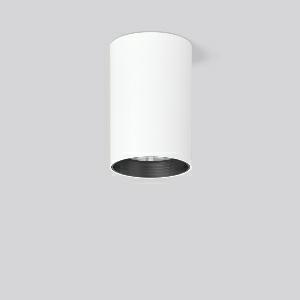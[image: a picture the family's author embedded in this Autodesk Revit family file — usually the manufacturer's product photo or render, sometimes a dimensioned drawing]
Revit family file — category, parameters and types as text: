
# Revit family: heledon_maxi_a_931229_002_3_b1d6
name_source: partatom
category: Lighting Fixtures
units: mm (PartAtom-declared; Revit-internal decimal feet)

## family parameters
Cut with Voids When Loaded = No
Host = Face
Light Source = No
Part Type = Normal
Room Calculation Point = No
Round Connector Dimension = Use Diameter
Shared = No

## types (1)
- HELEDON maxi A (1 x LED Modul 935, 3650 lm, 3500)
    Apparent Load = 35 VA
    Approval mark = CE
    CIE Flux Codes = 96 100 100 100 100
    Color Rendering = 92
    Color Temperature = 3500
    Default Elevation = 1800 mm
    Description = Series: HELEDON maxi
Cylindrical surface-mounted downlight. Housing: die-cast aluminium, powder-coated. Internal ceiling frame polycarbonate with bayonet mounting. Black plastic ring and recessed LED to prevent glare from the side. Optical assembly with lens made of plastic (polycarbonate) for the best homogeneous light distribution - can be changed without tools. Best colour rendering index Ra>90. Suitable for Ceiling mounting. Easy installation with a separate ceiling frame with bayonet mounting and plug connection. Driver integrated. Connected via plug-in connector. High quality converter without flickering and stroboscopic effect. The following accessories can be mounted without use of tools: interchangeable lenses, decorative glasses, honeycomb louvre, clear and frosted diffusers, white interchangeable plastic ring. 
Colour: traffic white, matt (RAL 9016)
Diameter: 123 mm
Height: 183 mm
Lamp: LED
Socket: without socket
Colour temperature: 3500K
Colour rendering index (CRI): 92
System power: 35 W
Rated luminous flux: 3650 lm
Luminous efficiency: 104 lm/W
Control gear: Regulated power supply
Protection class: I
Type of protection: IP 20
    Height = 183 mm
    Lamp = 1 x LED Modul 935
    Lamp Light Flux = 3650 lm
    Lamp count = 1
    Length = 123 mm
    Lifetime = 50000 h
    Luminous efficacy = 104 lm/W
    Manufacturer = RZB
    ModVariant = No
    Model = 931229.002.3
    Mounting Place = Ceiling
    Mounting Type = Surface mounted
    Number of Poles = 1
    OnlyDefault = Yes
    Power Factor = 1
    Product Name = HELEDON maxi A
    Product group = Surface mounted downlights
    ProductGroupID = 302
    Protection Class = Protection class I
    Protection Degree = IP 20
    RLX_Detail_Level = 1
    RLX_Emergency_Light_Flux = 0 lm
    RLX_Emergency_Type = 0
    RLX_Emergency_Type_DB = No
    RlxData = <blob elided: 98385 chars, md5=7ed885de>
    Socket = socket
    Standby Power = 0 W
    System Light Flux = 3650 lm
    System Power = 35 W
    Type Comments = Product without accessories
    Type Image = 931193.002.jpg
    URL = http://relux.com
    VarID = ---
    Voltage = 230 V
    Voltage Range = 220-240 V
    Weight = 0.00 kg
    Width = 0 mm  [stored 0 ft]

note: [stored X ft] marks values corroborated as IEEE doubles in the binary element streams (Revit-internal decimal feet)

## geometry (parser evidence)
native form markers: Blend x4, Sweep x10
no freeform markers — native parametric forms only
